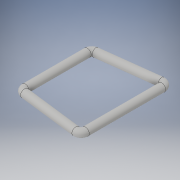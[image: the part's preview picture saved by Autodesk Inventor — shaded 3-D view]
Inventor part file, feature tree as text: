
AUTODESK INVENTOR PART (.ipt)
format: ipt  version: 2019 (Build 230136000, 136)  size: 160,256 bytes
history: native  units: mm
features: other x14, sketch x8, extrude x4, revolve x4
ambient origin geometry x8: Origin, YZ Plane, XZ Plane, XY Plane, X Axis, Y Axis, Z Axis, Center Point
bodies: Solid1 (feature_tree)
feature tree (30):
  extrude  "Extrusion1"  Depth=16.929694mm
  revolve  "Revolution1"  [1 undecoded]
  revolve  "Revolution2"  [1 undecoded]
  sketch  "Sketch_8"
  extrude  "Extrusion2"  Depth=12.015472mm TaperAngle=0.0deg
  extrude  "Extrusion3"  [1 undecoded]
  revolve  "Revolution3"  [1 undecoded]
  revolve  "Revolution4"  [1 undecoded]
  extrude  "Extrusion4"  [1 undecoded]
  other  "B_XY"
  other  "B_YZ"
  other  "B_ZX"
  other  "B_X"
  other  "B_Y"
  other  "B_Z"
  other  "B_Center"
  other  "C_XY"
  other  "C_YZ"
  other  "C_ZX"
  other  "C_X"
  other  "C_Y"
  other  "C_Z"
  other  "C_Center"
  sketch  "Sketch_1"  dims[d0=14.8mm d1=0.0mm d2=16.929694mm]
  sketch  "Sketch_2"  dims[d3=16.929694mm d4=11.42425mm d5=0.0mm]
  sketch  "Sketch_3"  dims[d6=11.42425mm d7=0.0mm d8=14.486233mm]
  sketch  "Sketch_4"  dims[d9=14.486233mm d10=12.015472mm d11=0.0mm]
  sketch  "Sketch_5"
  sketch  "Sketch_6"
  sketch  "Sketch_7"
note: 6 required parameter values undecoded (feature->parameter linkage not recoverable at this tier; creation-order binding heuristic only, values carry confidence <= 0.55)